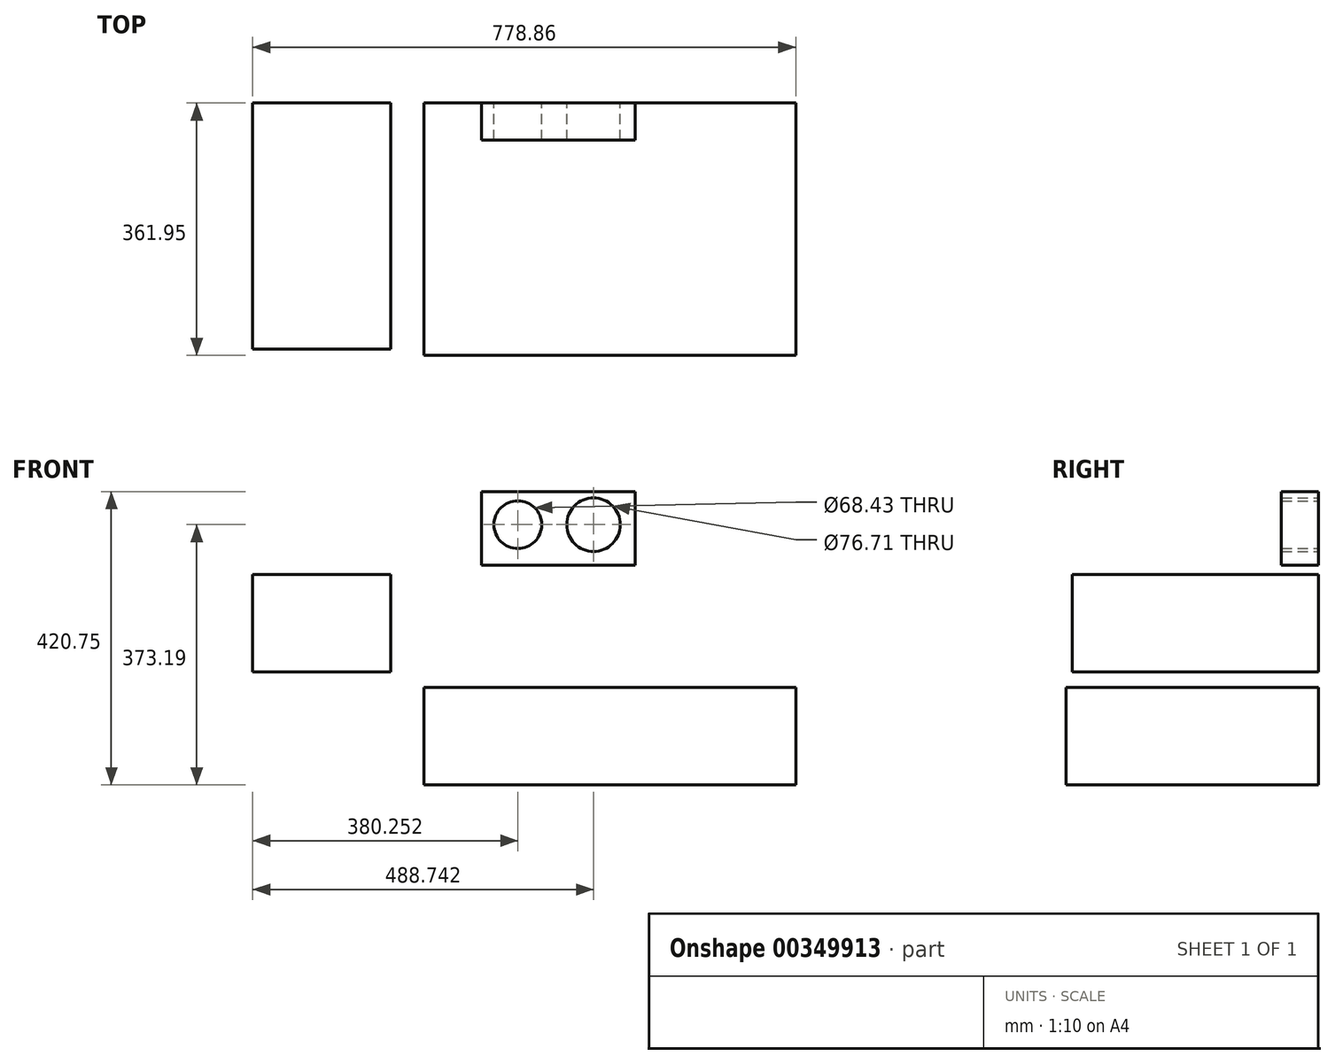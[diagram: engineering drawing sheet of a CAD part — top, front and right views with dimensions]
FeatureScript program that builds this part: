
annotation { "Feature Type Name" : "Feature", "Feature Type Description" : "" }
export const myFeature = defineFeature(function(context is Context, id is Id, definition is map)
    precondition{}
    {
        {
            var Q0;
            Q0=qCreatedBy(makeId("Front.planeOp"),FACE);
            var sketch = newSketch(context, id + "F0", { "sketchPlane" : qUnion([Q0])});
            skLineSegment(sketch, "E0.bottom", {"start": v(-76.85, 99.85) * mm, "end": v(121.27, 99.85) * mm});
            skLineSegment(sketch, "E0.top", {"start": v(-76.85, -39.85) * mm, "end": v(121.27, -39.85) * mm});
            skLineSegment(sketch, "E0.left", {"start": v(-76.85, 99.85) * mm, "end": v(-76.85, -39.85) * mm});
            skLineSegment(sketch, "E0.right", {"start": v(121.27, 99.85) * mm, "end": v(121.27, -39.85) * mm});
            skSolve(sketch);
        }
        {
            var Q0;
            Q0 = qSketchRegion(id + "F0", true);
            extrude(context, id + "F1", {"entities" : qUnion([Q0]), "depth" : 353.06 * mm, "offsetDistance" : 25.4 * mm});
        }
        {
            var Q0;
            Q0=qCreatedBy(makeId("Front.planeOp"),FACE);
            var sketch = newSketch(context, id + "F2", { "sketchPlane" : qUnion([Q0])});
            skLineSegment(sketch, "E1.bottom", {"start": v(87.33, -61.96) * mm, "end": v(620.73, -61.96) * mm});
            skLineSegment(sketch, "E1.top", {"start": v(87.33, -201.66) * mm, "end": v(620.73, -201.66) * mm});
            skLineSegment(sketch, "E1.left", {"start": v(87.33, -61.96) * mm, "end": v(87.33, -201.66) * mm});
            skLineSegment(sketch, "E1.right", {"start": v(620.73, -61.96) * mm, "end": v(620.73, -201.66) * mm});
            skSolve(sketch);
        }
        {
            var Q0;
            Q0 = qSketchRegion(id + "F2", true);
            extrude(context, id + "F3", {"entities" : qUnion([Q0]), "depth" : 361.95 * mm, "offsetDistance" : 25.4 * mm});
        }
        {
            var Q0;
            Q0=makeQuery(id+"F3.opExtrude","SWEPT_BODY",BODY,{"disambiguationData":[OSD([sQuery(id+"F2.wireOp",EDGE,"E1.bottom"),sQuery(id+"F2.wireOp",EDGE,"E1.top"),sQuery(id+"F2.wireOp",EDGE,"E1.left"),sQuery(id+"F2.wireOp",EDGE,"E1.right")])]});
            transform(context, id + "F4", {"entities" : qUnion([Q0]), "transformType" : TransformType.TRANSLATION_3D, "dx" : 81.28 * mm, "dy" : 0 * mm, "dz" : 0 * mm, "makeCopy" : false});
        }
        {
            var Q0;
            Q0=qCreatedBy(makeId("Front.planeOp"),FACE);
            var sketch = newSketch(context, id + "F5", { "sketchPlane" : qUnion([Q0])});
            skLineSegment(sketch, "E2.bottom", {"start": v(251.39, 219.09) * mm, "end": v(471.34, 219.09) * mm});
            skLineSegment(sketch, "E2.top", {"start": v(251.39, 113.57) * mm, "end": v(471.34, 113.57) * mm});
            skLineSegment(sketch, "E2.left", {"start": v(251.39, 219.09) * mm, "end": v(251.39, 113.57) * mm});
            skLineSegment(sketch, "E2.right", {"start": v(471.34, 219.09) * mm, "end": v(471.34, 113.57) * mm});
            skCircle(sketch, "E3", {"center": v(303.4, 171.53) * mm, "radius": 34.21 * mm});
            skCircle(sketch, "E4", {"center": v(411.9, 171.53) * mm, "radius": 38.35 * mm});
            skSolve(sketch);
        }
        {
            var Q0;
            Q0 = qSketchRegion(id + "F5", true);
            extrude(context, id + "F6", {"entities" : qUnion([Q0]), "depth" : 53.34 * mm, "offsetDistance" : 25.4 * mm});
        }
    });
